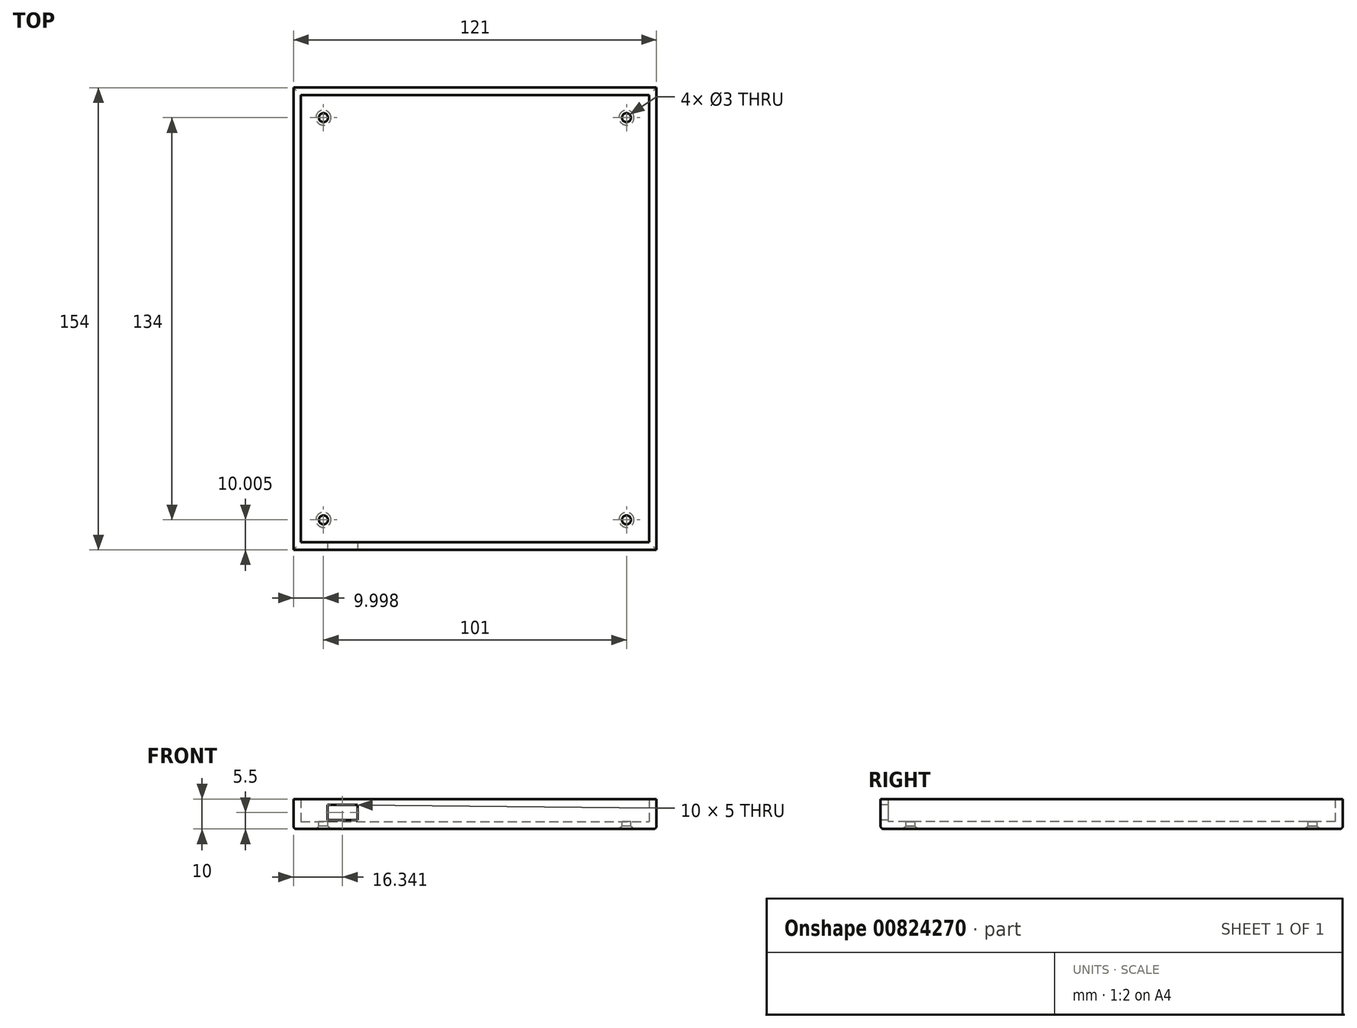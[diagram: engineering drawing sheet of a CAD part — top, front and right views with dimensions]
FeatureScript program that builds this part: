
annotation { "Feature Type Name" : "Feature", "Feature Type Description" : "" }
export const myFeature = defineFeature(function(context is Context, id is Id, definition is map)
    precondition{}
    {
        {
            var Q0;
            Q0=qCreatedBy(makeId("Top.planeOp"),FACE);
            var sketch = newSketch(context, id + "F0", { "sketchPlane" : qUnion([Q0])});
            skLineSegment(sketch, "E0.bottom", {"start": v(-90.74, 109.84) * mm, "end": v(30.26, 109.84) * mm});
            skLineSegment(sketch, "E0.top", {"start": v(-90.74, -44.16) * mm, "end": v(30.26, -44.16) * mm});
            skLineSegment(sketch, "E0.left", {"start": v(-90.74, 109.84) * mm, "end": v(-90.74, -44.16) * mm});
            skLineSegment(sketch, "E0.right", {"start": v(30.26, 109.84) * mm, "end": v(30.26, -44.16) * mm});
            skSolve(sketch);
        }
        {
            var Q0;
            Q0=makeQuery(id+"F0.imprint","IMPRINT",FACE,{"disambiguationData":[TD([[makeQuery(id+"F0.imprint","IMPRINT",EDGE,{"derivedFrom":sQuery(id+"F0.wireOp",EDGE,"E0.bottom")}),-1.0]])]});
            extrude(context, id + "F1", {"entities" : qUnion([Q0]), "depth" : 10 * mm, "offsetDistance" : 25 * mm});
        }
        {
            var Q0;
            Q0=makeQuery(id+"F1.opExtrude","CAP_FACE",FACE,{"disambiguationData":[OSD([sQuery(id+"F0.wireOp",EDGE,"E0.bottom"),sQuery(id+"F0.wireOp",EDGE,"E0.top"),sQuery(id+"F0.wireOp",EDGE,"E0.left"),sQuery(id+"F0.wireOp",EDGE,"E0.right")])],"isStart":false});
            shell(context, id + "F2", {"entities" : qUnion([Q0]), "thickness" : 2.5 * mm});
        }
        {
            var Q0;
            Q0=makeQuery(id+"F1.opExtrude","CAP_FACE",FACE,{"disambiguationData":[OSD([sQuery(id+"F0.wireOp",EDGE,"E0.bottom"),sQuery(id+"F0.wireOp",EDGE,"E0.top"),sQuery(id+"F0.wireOp",EDGE,"E0.left"),sQuery(id+"F0.wireOp",EDGE,"E0.right")])],"isStart":true});
            var sketch = newSketch(context, id + "F3", { "sketchPlane" : qUnion([Q0])});
            skPoint(sketch, "E1", {"position": v(-80.74, 34.16) * mm});
            skPoint(sketch, "E2", {"position": v(20.26, 34.16) * mm});
            skPoint(sketch, "E3", {"position": v(-80.74, -99.84) * mm});
            skPoint(sketch, "E4", {"position": v(20.26, -99.84) * mm});
            skSolve(sketch);
        }
        {
            var Q0;
            Q0=sQuery(id+"F3.wireOp",VERTEX,"E1");
            var Q1;
            Q1=sQuery(id+"F3.wireOp",VERTEX,"E2");
            var Q2;
            Q2=sQuery(id+"F3.wireOp",VERTEX,"E3");
            var Q3;
            Q3=sQuery(id+"F3.wireOp",VERTEX,"E4");
            var Q4;
            Q4=makeQuery(id+"F1.opExtrude","SWEPT_BODY",BODY,{"disambiguationData":[OSD([sQuery(id+"F0.wireOp",EDGE,"E0.bottom"),sQuery(id+"F0.wireOp",EDGE,"E0.top"),sQuery(id+"F0.wireOp",EDGE,"E0.left"),sQuery(id+"F0.wireOp",EDGE,"E0.right")])]});
            hole(context, id + "F4", {"style" : HoleStyle.C_SINK, "endStyle" : HoleEndStyle.THROUGH, "holeDiameter" : 3 * mm, "cSinkDiameter" : 5 * mm, "cSinkAngle" : 90 * degree, "majorDiameter" : 5 * mm, "isTappedThrough" : true, "tappedDepth" : 12 * mm, "tapClearance" : 3, "locations" : qUnion([Q0, Q1, Q2, Q3]), "scope" : qUnion([Q4]), "startStyle" : HoleStartStyle.PART});
        }
        {
            var Q0;
            Q0=makeQuery(id+"F1.opExtrude","CAP_EDGE",EDGE,{"disambiguationData":[OSD([sQuery(id+"F0.wireOp",EDGE,"E0.top")])],"isStart":true});
            var Q1;
            Q1=makeQuery(id+"F1.opExtrude","CAP_EDGE",EDGE,{"disambiguationData":[OSD([sQuery(id+"F0.wireOp",EDGE,"E0.left")])],"isStart":true});
            var Q2;
            Q2=makeQuery(id+"F1.opExtrude","CAP_EDGE",EDGE,{"disambiguationData":[OSD([sQuery(id+"F0.wireOp",EDGE,"E0.right")])],"isStart":true});
            var Q3;
            Q3=makeQuery(id+"F1.opExtrude","CAP_EDGE",EDGE,{"disambiguationData":[OSD([sQuery(id+"F0.wireOp",EDGE,"E0.bottom")])],"isStart":true});
            fillet(context, id + "F5", {"entities" : qUnion([Q0, Q1, Q2, Q3]), "radius" : 1 * mm, "tangentPropagation" : true, "allowEdgeOverflow" : false});
        }
        {
            var Q0;
            Q0=makeQuery(id+"F1.opExtrude","SWEPT_FACE",FACE,{"disambiguationData":[OSD([sQuery(id+"F0.wireOp",EDGE,"E0.top")])]});
            var sketch = newSketch(context, id + "F6", { "sketchPlane" : qUnion([Q0])});
            skLineSegment(sketch, "E5.bottom", {"start": v(-69.4, 8) * mm, "end": v(-79.4, 8) * mm});
            skLineSegment(sketch, "E5.top", {"start": v(-69.4, 3) * mm, "end": v(-79.4, 3) * mm});
            skLineSegment(sketch, "E5.left", {"start": v(-69.4, 8) * mm, "end": v(-69.4, 3) * mm});
            skLineSegment(sketch, "E5.right", {"start": v(-79.4, 8) * mm, "end": v(-79.4, 3) * mm});
            skPoint(sketch, "E5.middle", {"position": v(-74.4, 5.5) * mm});
            skPoint(sketch, "E5.middle.positionSnap0", {"position": v(-90.74, 5.5) * mm});
            skPoint(sketch, "E5.centerSnap0", {"position": v(-90.74, 5.5) * mm});
            skSolve(sketch);
        }
        {
            var Q0;
            Q0=qSketchRegion(id+"F6",true);
            var Q1;
            Q1=makeQuery(id+"F2.opShell","OFFSET_FACE",FACE,{"disambiguationData":[OSD([sQuery(id+"F0.wireOp",EDGE,"E0.top")])]});
            extrude(context, id + "F7", {"entities" : qUnion([Q0]), "operationType" : NewBodyOperationType.REMOVE, "endBound" : BoundingType.UP_TO_SURFACE, "oppositeDirection" : true, "depth" : 5 * mm, "endBoundEntityFace" : qUnion([Q1]), "offsetDistance" : 25 * mm});
        }
    });
